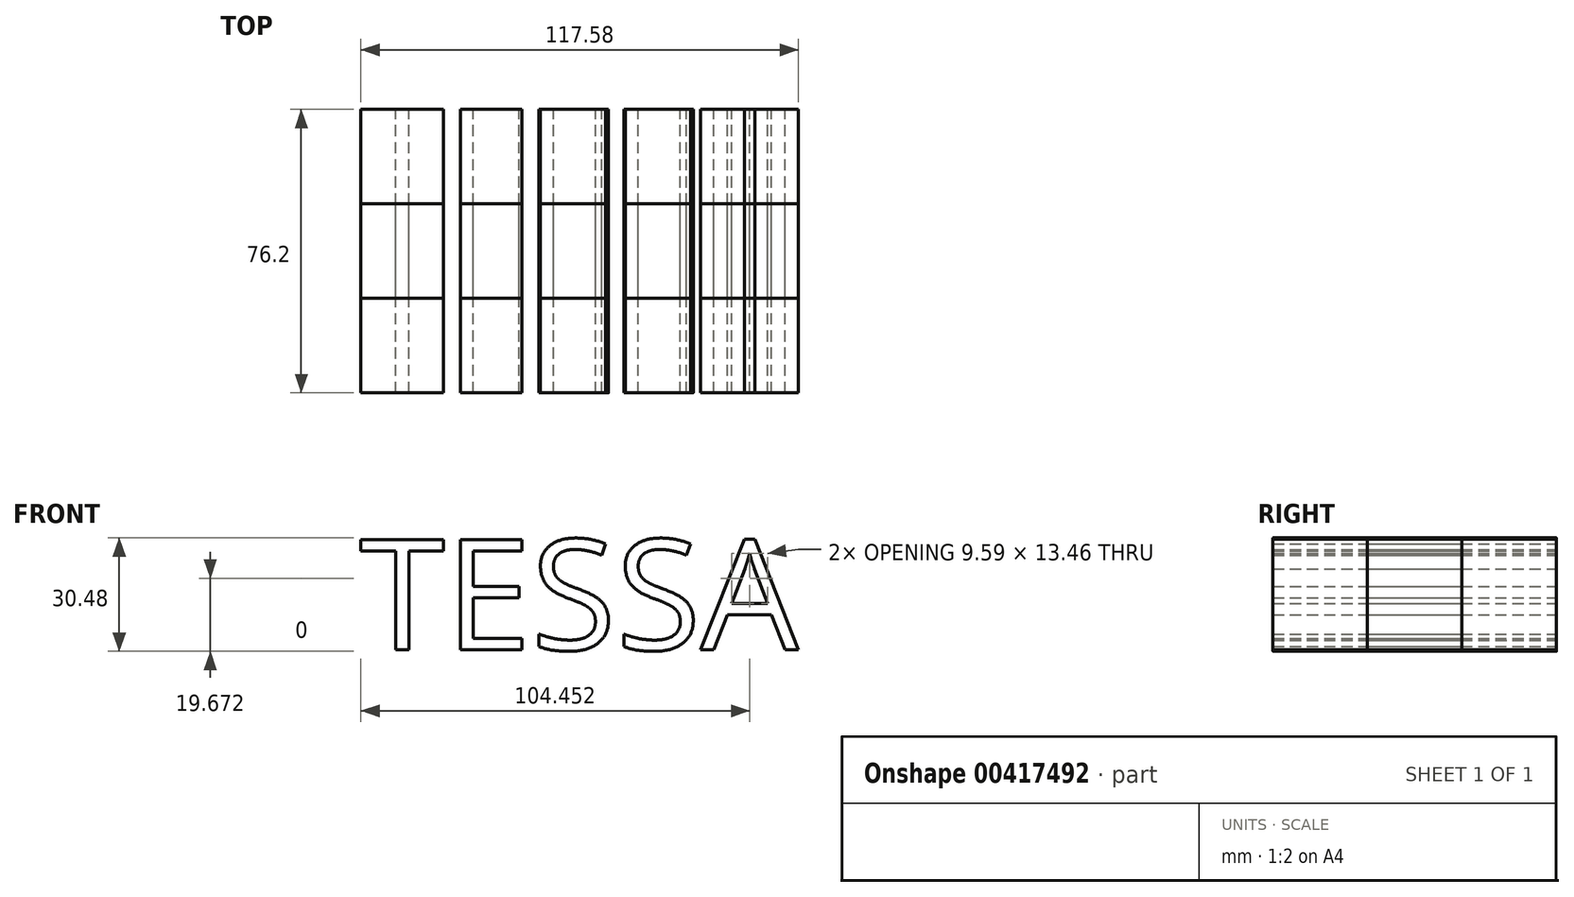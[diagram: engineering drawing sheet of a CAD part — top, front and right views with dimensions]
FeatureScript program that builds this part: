
annotation { "Feature Type Name" : "Feature", "Feature Type Description" : "" }
export const myFeature = defineFeature(function(context is Context, id is Id, definition is map)
    precondition{}
    {
        {
            var Q0;
            Q0=qCreatedBy(makeId("Front.planeOp"),FACE);
            var sketch = newSketch(context, id + "F0", { "sketchPlane" : qUnion([Q0])});
            skText(sketch, "E0", { "text": "TESSA", "fontName": "OpenSans-Regular.ttf"});
            const initialGuessF0  = {"E0": [0, -0.0299, 1, 0, 0.0299]};
            skSetInitialGuess(sketch, initialGuessF0);
            skSolve(sketch);
        }
        {
            var Q0;
            Q0 = qSketchRegion(id + "F0", true);
            extrude(context, id + "F1", {"entities" : qUnion([Q0]), "endBound" : BoundingType.SYMMETRIC, "depth" : 25.4 * mm});
        }
        {
            var Q0;
            Q0 = qSketchRegion(id + "F0", true);
            extrude(context, id + "F2", {"entities" : qUnion([Q0]), "endBound" : BoundingType.SYMMETRIC, "depth" : 76.2 * mm});
        }
    });
